# Revit family: Digital_Media-Honeywell-Audio_Player-X-MAP04
name_source: partatom
category: Electrical Equipment
revit_build: Autodesk Revit 2017 (Build: 20160225_1515(x64)
units: mm (PartAtom-declared; Revit-internal decimal feet)

## family parameters
Cut with Voids When Loaded = No
Host = Face
OmniClass Number = 23.85.50.00
OmniClass Title = Communication Systems
Part Type = Equipment Switch
Room Calculation Point = No
Round Connector Dimension = Use Diameter
Shared = No

## types (1)
- Audio Player - X-MAP04
    Apparent Load = 0 VA
    Default Elevation = 1219 mm
    Depth = 252 mm  [stored 0.826772 ft]
    Description = DVD/CD/MP3/FM/AM audio player
    Finish = Metal - Honeywell - Stainless Steel - Black
    Frequency = 47 Hz
    Height = 44 mm  [stored 0.144357 ft]
    Inputs = FM 75 Ω, USB-Port, SD-Port
    Load Sub-Classification = No
    Manufacturer = Honeywell International
    Manufacturer Fax Number = 02131/40615-606
    Model = X-MAP04
    Number of Poles = 1
    Outputs = 1 x Cinch for FM/AM-Tuner, 1 x Cinch for DVD/USB/SD, 1 x Cinch for mixed signals
    Power Consumption = 13 W
    Power Factor = 1
    Product Documentation Link = https://www.esser-systems.com
    Product Name = Audio Player
    Product Page URL = https://www.esser-systems.com
    Rated Voltage = 230 V AC
    URL = www.esser-systems.com
    Utility = No
    Version = 2017 - v1.0a
    Voltage = 230 V
    Wattage = 13 W
    Watts = 13 W
    Weight = 3.80 kgf
    Width = 482 mm  [stored 1.58136 ft]

note: [stored X ft] marks values corroborated as IEEE doubles in the binary element streams (Revit-internal decimal feet)

## geometry (parser evidence)
native form markers: Sweep x2
no freeform markers — native parametric forms only
